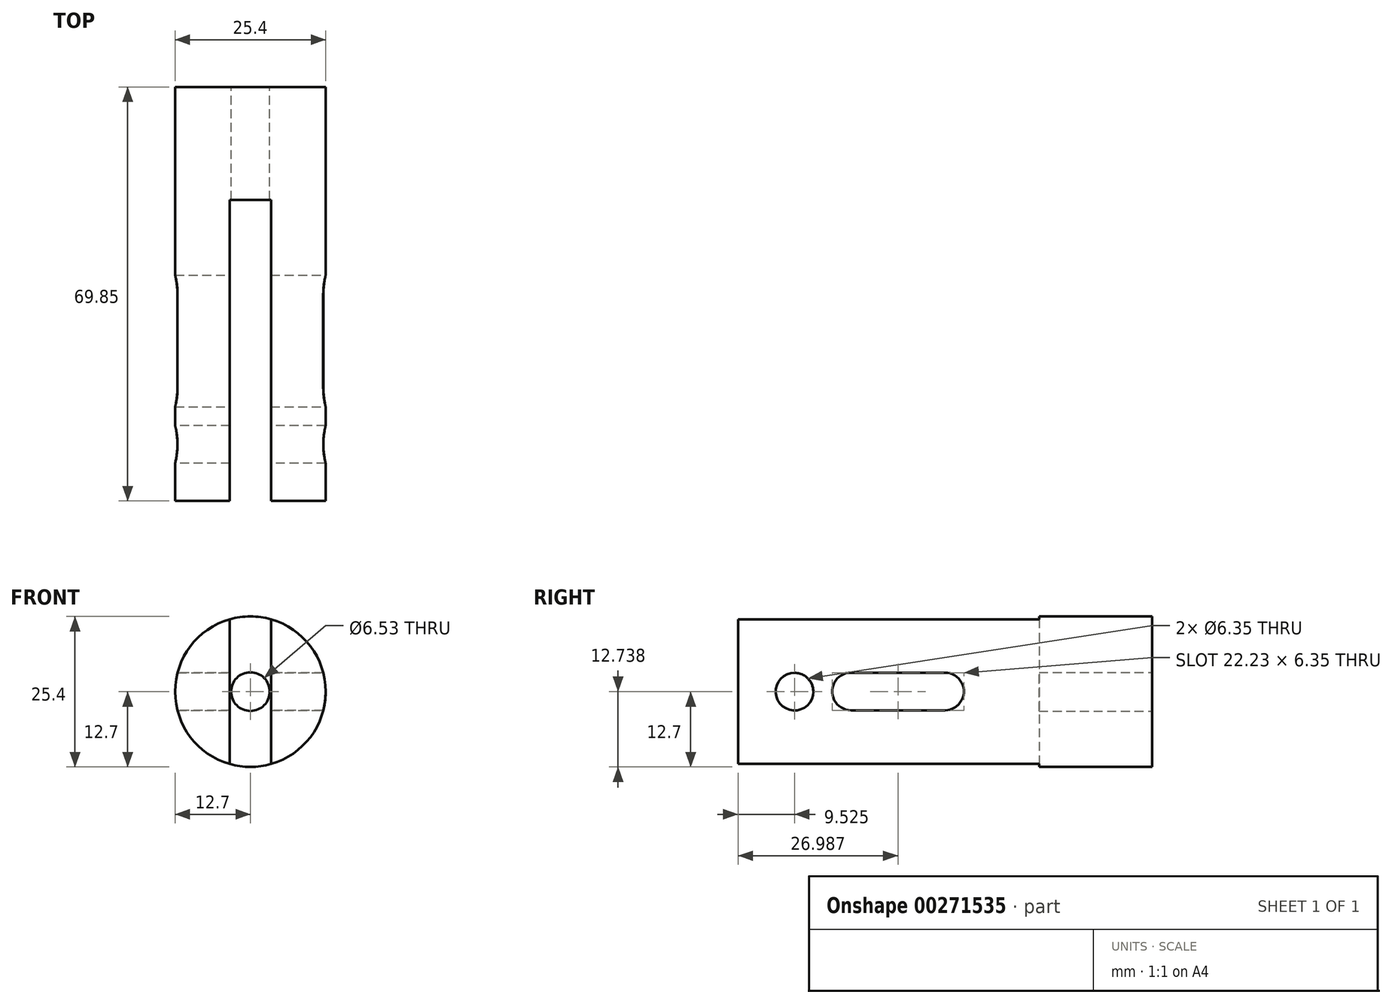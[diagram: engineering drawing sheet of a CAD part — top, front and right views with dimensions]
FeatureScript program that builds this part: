
annotation { "Feature Type Name" : "Feature", "Feature Type Description" : "" }
export const myFeature = defineFeature(function(context is Context, id is Id, definition is map)
    precondition{}
    {
        {
            var Q0;
            Q0=qCreatedBy(makeId("Front.planeOp"),FACE);
            var sketch = newSketch(context, id + "F0", { "sketchPlane" : qUnion([Q0])});
            skCircle(sketch, "E0", {"center": v(0, 0) * mm, "radius": 12.7 * mm});
            skSolve(sketch);
        }
        {
            var Q0;
            Q0=makeQuery(id+"F0.imprint","IMPRINT",FACE,{"disambiguationData":[TD([[makeQuery(id+"F0.imprint","IMPRINT",EDGE,{"derivedFrom":sQuery(id+"F0.wireOp",EDGE,"E0")}),1.0]])]});
            extrude(context, id + "F1", {"entities" : qUnion([Q0]), "depth" : 69.85 * mm, "offsetDistance" : 25.4 * mm});
        }
        {
            var Q0;
            Q0=sQuery(id+"F0.wireOp",VERTEX,"E0.center");
            var Q1;
            Q1=makeQuery(id+"F1.opExtrude","SWEPT_BODY",BODY,{"disambiguationData":[OSD([sQuery(id+"F0.wireOp",EDGE,"E0")])]});
            hole(context, id + "F2", {"style" : HoleStyle.SIMPLE, "endStyle" : HoleEndStyle.THROUGH, "oppositeDirection" : true, "standardTappedOrClearance" : lookupTablePath({ "standard" : "ANSI", "engagement" : "75%", "pitch" : "18 tpi", "size" : "5/16", "type" : "Tapped" }), "standardBlindInLast" : lookupTablePath({ "standard" : "ANSI", "engagement" : "75%", "pitch" : "18 tpi", "size" : "5/16", "type" : "Tapped" }), "holeDiameter" : 6.53 * mm, "showTappedDepth" : true, "tappedDepth" : 25.4 * mm, "tapClearance" : 3, "locations" : qUnion([Q0]), "scope" : qUnion([Q1]), "majorDiameter" : 7.94 * mm});
        }
        {
            var Q0;
            Q0=makeQuery(id+"F1.opExtrude","CAP_FACE",FACE,{"disambiguationData":[OSD([sQuery(id+"F0.wireOp",EDGE,"E0")])],"isStart":false});
            var sketch = newSketch(context, id + "F3", { "sketchPlane" : qUnion([Q0])});
            skLineSegment(sketch, "E1.0", {"start": v(-3.48, 12.7) * mm, "end": v(-3.48, -12.7) * mm});
            skLineSegment(sketch, "E2.0", {"start": v(3.48, 12.7) * mm, "end": v(3.48, -12.7) * mm});
            skLineSegment(sketch, "E3", {"start": v(-3.48, 12.7) * mm, "end": v(3.48, 12.7) * mm});
            skLineSegment(sketch, "E4", {"start": v(-3.48, -12.7) * mm, "end": v(3.48, -12.7) * mm});
            skSolve(sketch);
        }
        {
            var Q0;
            {var subQ1=sQuery(id+"F0.wireOp",EDGE,"E0");var subQ2=makeQuery(id+"F1.opExtrude","CAP_EDGE",EDGE,{"disambiguationData":[OSD([subQ1])],"isStart":false});var subQ5=sQuery(id+"F3.wireOp",EDGE,"E1.0");var subQ6=makeQuery(id+"F3.imprint","INTERSECT",VERTEX,{"disambiguationData":[OD(1.0)],"derivedFrom":[subQ2,subQ5]});Q0=makeQuery(id+"F3.imprint","IMPRINT",FACE,{"disambiguationData":[TD([[makeQuery(id+"F3.imprint","IMPRINT",EDGE,{"disambiguationData":[TD([[subQ6,-1.0]])],"derivedFrom":subQ2}),1.0]])]});}
            var Q1;
            {var subQ1=sQuery(id+"F0.wireOp",EDGE,"E0");var subQ2=makeQuery(id+"F1.opExtrude","CAP_EDGE",EDGE,{"disambiguationData":[OSD([subQ1])],"isStart":false});var subQ5=sQuery(id+"F3.wireOp",EDGE,"E1.0");var subQ9=makeQuery(id+"F3.imprint","INTERSECT",VERTEX,{"disambiguationData":[OD(0.0)],"derivedFrom":[subQ2,subQ5]});Q1=makeQuery(id+"F3.imprint","IMPRINT",FACE,{"disambiguationData":[TD([[makeQuery(id+"F3.imprint","IMPRINT",EDGE,{"disambiguationData":[TD([[subQ9,1.0]])],"derivedFrom":subQ2}),1.0]])]});}
            var Q2;
            Q2=sQuery(id+"F3.wireOp",EDGE,"E1.0");
            var Q3;
            Q3=sQuery(id+"F3.wireOp",EDGE,"E3");
            var Q4;
            Q4=sQuery(id+"F3.wireOp",EDGE,"E2.0");
            var Q5;
            Q5=sQuery(id+"F3.wireOp",EDGE,"E4");
            extrude(context, id + "F4", {"entities" : qUnion([Q0, Q1]), "operationType" : NewBodyOperationType.REMOVE, "surfaceEntities" : qUnion([Q2, Q3, Q4, Q5]), "oppositeDirection" : true, "depth" : 50.8 * mm, "offsetDistance" : 25.4 * mm});
        }
        {
            var Q0;
            Q0=qCreatedBy(makeId("Right.planeOp"),FACE);
            var sketch = newSketch(context, id + "F5", { "sketchPlane" : qUnion([Q0])});
            skCircle(sketch, "E5", {"center": v(-60.33, 0) * mm, "radius": 3.18 * mm});
            skSolve(sketch);
        }
        {
            var Q0;
            Q0 = qSketchRegion(id + "F5", true);
            extrude(context, id + "F6", {"entities" : qUnion([Q0]), "operationType" : NewBodyOperationType.REMOVE, "endBound" : BoundingType.SYMMETRIC, "depth" : 25.4 * mm});
        }
        {
            var Q0;
            Q0=qCreatedBy(makeId("Right.planeOp"),FACE);
            var sketch = newSketch(context, id + "F7", { "sketchPlane" : qUnion([Q0])});
            skLineSegment(sketch, "E6.bottom", {"start": v(-50.8, 3.21) * mm, "end": v(-34.93, 3.21) * mm});
            skLineSegment(sketch, "E6.top", {"start": v(-50.8, -3.14) * mm, "end": v(-34.93, -3.14) * mm});
            skArc(sketch, "E7", {"start": v(-34.93, -3.14) * mm, "mid": v(-31.75, 0.04) * mm, "end": v(-34.93, 3.21) * mm});
            skArc(sketch, "E8", {"start": v(-50.8, 3.21) * mm, "mid": v(-53.98, 0.04) * mm, "end": v(-50.8, -3.14) * mm});
            skSolve(sketch);
        }
        {
            var Q0;
            Q0=makeQuery(id+"F7.imprint","IMPRINT",FACE,{"disambiguationData":[TD([[makeQuery(id+"F7.imprint","IMPRINT",EDGE,{"derivedFrom":sQuery(id+"F7.wireOp",EDGE,"E6.bottom")}),-1.0]])]});
            extrude(context, id + "F8", {"entities" : qUnion([Q0]), "operationType" : NewBodyOperationType.REMOVE, "endBound" : BoundingType.SYMMETRIC, "oppositeDirection" : true, "depth" : 25.4 * mm, "offsetDistance" : 25.4 * mm});
        }
    });
